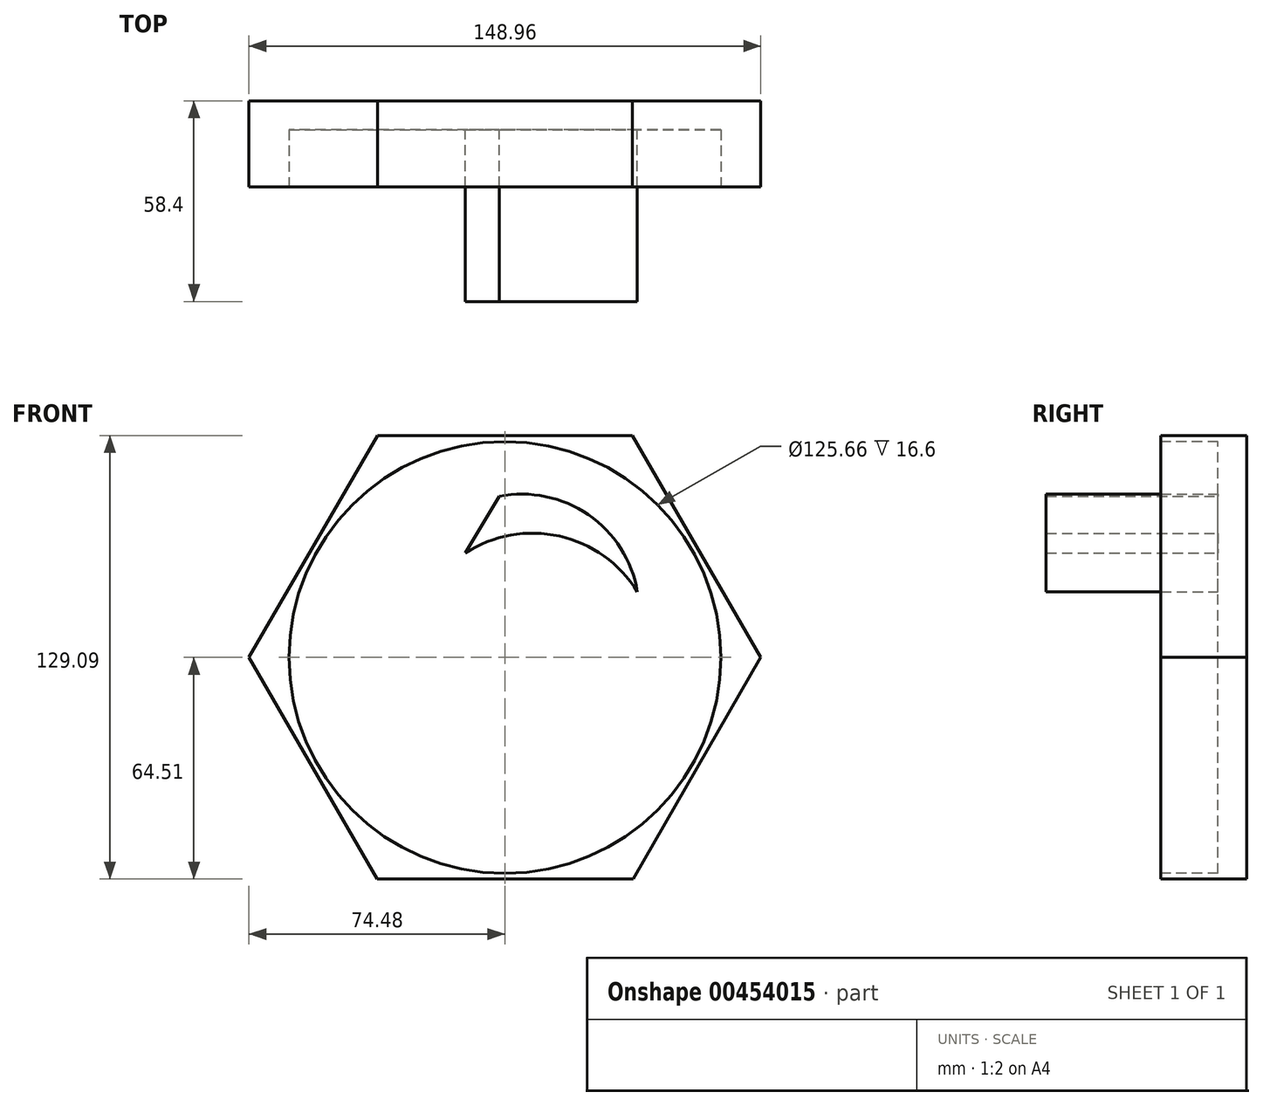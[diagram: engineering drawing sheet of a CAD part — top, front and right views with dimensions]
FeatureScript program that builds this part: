
annotation { "Feature Type Name" : "Feature", "Feature Type Description" : "" }
export const myFeature = defineFeature(function(context is Context, id is Id, definition is map)
    precondition{}
    {
        {
            var Q0;
            Q0=qCreatedBy(makeId("Front.planeOp"),FACE);
            var sketch = newSketch(context, id + "F0", { "sketchPlane" : qUnion([Q0])});
            skCircle(sketch, "E0", {"center": v(0, 0) * mm, "radius": 74.48 * mm, "construction": true});
            skLineSegment(sketch, "E1", {"start": v(0, 0) * mm, "end": v(74.48, 0) * mm});
            skLineSegment(sketch, "E2", {"start": v(0, 0) * mm, "end": v(37.11, 64.58) * mm});
            skLineSegment(sketch, "E3", {"start": v(-37.11, 64.58) * mm, "end": v(0, 0) * mm});
            skLineSegment(sketch, "E4", {"start": v(0, 0) * mm, "end": v(-74.48, 0) * mm});
            skLineSegment(sketch, "E5", {"start": v(0, 0) * mm, "end": v(-37.24, -64.5) * mm});
            skLineSegment(sketch, "E6", {"start": v(0, 0) * mm, "end": v(37.37, -64.43) * mm});
            skLineSegment(sketch, "E7", {"start": v(-37.24, -64.5) * mm, "end": v(37.37, -64.43) * mm});
            skLineSegment(sketch, "E8", {"start": v(37.37, -64.43) * mm, "end": v(74.48, 0) * mm});
            skLineSegment(sketch, "E9", {"start": v(74.48, 0) * mm, "end": v(37.11, 64.58) * mm});
            skLineSegment(sketch, "E10", {"start": v(37.11, 64.58) * mm, "end": v(-37.11, 64.58) * mm});
            skLineSegment(sketch, "E11", {"start": v(-37.11, 64.58) * mm, "end": v(-74.48, 0) * mm});
            skLineSegment(sketch, "E12", {"start": v(-74.48, 0) * mm, "end": v(-37.24, -64.5) * mm});
            skSolve(sketch);
        }
        {
            var Q0;
            Q0=makeQuery(id+"F0.imprint","IMPRINT",FACE,{"disambiguationData":[TD([[makeQuery(id+"F0.imprint","IMPRINT",EDGE,{"derivedFrom":sQuery(id+"F0.wireOp",EDGE,"E3")}),-1.0]])]});
            var Q1;
            Q1=makeQuery(id+"F0.imprint","IMPRINT",FACE,{"disambiguationData":[TD([[makeQuery(id+"F0.imprint","IMPRINT",EDGE,{"derivedFrom":sQuery(id+"F0.wireOp",EDGE,"E2")}),1.0]])]});
            var Q2;
            Q2=makeQuery(id+"F0.imprint","IMPRINT",FACE,{"disambiguationData":[TD([[makeQuery(id+"F0.imprint","IMPRINT",EDGE,{"derivedFrom":sQuery(id+"F0.wireOp",EDGE,"E1")}),1.0]])]});
            var Q3;
            Q3=makeQuery(id+"F0.imprint","IMPRINT",FACE,{"disambiguationData":[TD([[makeQuery(id+"F0.imprint","IMPRINT",EDGE,{"derivedFrom":sQuery(id+"F0.wireOp",EDGE,"E1")}),-1.0]])]});
            var Q4;
            Q4=makeQuery(id+"F0.imprint","IMPRINT",FACE,{"disambiguationData":[TD([[makeQuery(id+"F0.imprint","IMPRINT",EDGE,{"derivedFrom":sQuery(id+"F0.wireOp",EDGE,"E5")}),1.0]])]});
            var Q5;
            Q5=makeQuery(id+"F0.imprint","IMPRINT",FACE,{"disambiguationData":[TD([[makeQuery(id+"F0.imprint","IMPRINT",EDGE,{"derivedFrom":sQuery(id+"F0.wireOp",EDGE,"E4")}),1.0]])]});
            extrude(context, id + "F1", {"entities" : qUnion([Q0, Q1, Q2, Q3, Q4, Q5]), "depth" : 25 * mm});
        }
        {
            var Q0;
            Q0=makeQuery(id+"F1.opExtrude","CAP_FACE",FACE,{"disambiguationData":[OSD([sQuery(id+"F0.wireOp",EDGE,"E7"),sQuery(id+"F0.wireOp",EDGE,"E8"),sQuery(id+"F0.wireOp",EDGE,"E9"),sQuery(id+"F0.wireOp",EDGE,"E10"),sQuery(id+"F0.wireOp",EDGE,"E11"),sQuery(id+"F0.wireOp",EDGE,"E12")])],"isStart":false});
            var sketch = newSketch(context, id + "F2", { "sketchPlane" : qUnion([Q0])});
            skCircle(sketch, "E13", {"center": v(0, 0) * mm, "radius": 62.83 * mm});
            skSolve(sketch);
        }
        {
            var Q0;
            Q0 = qSketchRegion(id + "F2", true);
            extrude(context, id + "F3", {"entities" : qUnion([Q0]), "operationType" : NewBodyOperationType.REMOVE, "oppositeDirection" : true, "depth" : 16.6 * mm});
        }
        {
            var Q0;
            Q0=makeQuery(id+"F3.boolean.opBoolean","COPY",FACE,{"derivedFrom":makeQuery(id+"F3.opExtrude","CAP_FACE",FACE,{"disambiguationData":[OSD([sQuery(id+"F2.wireOp",EDGE,"E13")])],"isStart":false})});
            var sketch = newSketch(context, id + "F4", { "sketchPlane" : qUnion([Q0])});
            skArc(sketch, "E14", {"start": v(38.55, 19.15) * mm, "mid": v(15.88, 35.3) * mm, "end": v(-11.52, 30.36) * mm});
            skLineSegment(sketch, "E15", {"start": v(-11.52, 30.36) * mm, "end": v(-1.66, 46.87) * mm});
            skArc(sketch, "E16", {"start": v(38.55, 19.15) * mm, "mid": v(24.32, 41.53) * mm, "end": v(-1.66, 46.87) * mm});
            skSolve(sketch);
        }
        {
            var Q0;
            Q0 = qSketchRegion(id + "F4", true);
            extrude(context, id + "F5", {"entities" : qUnion([Q0]), "operationType" : NewBodyOperationType.ADD, "depth" : 50 * mm});
        }
    });
